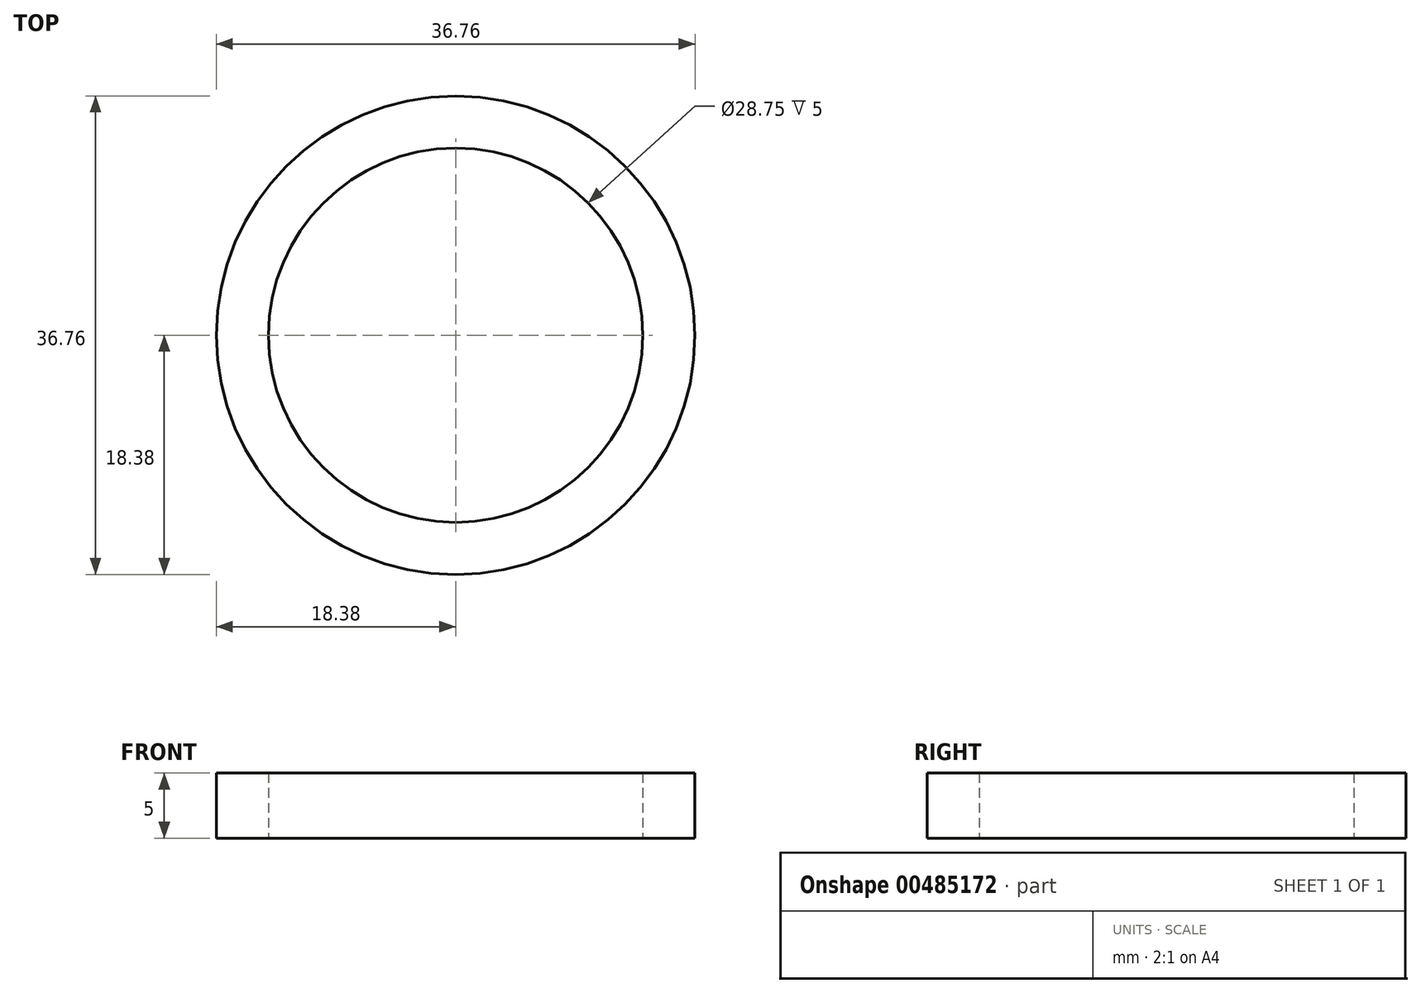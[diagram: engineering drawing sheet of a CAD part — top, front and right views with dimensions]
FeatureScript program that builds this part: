
annotation { "Feature Type Name" : "Feature", "Feature Type Description" : "" }
export const myFeature = defineFeature(function(context is Context, id is Id, definition is map)
    precondition{}
    {
        {
            var Q0;
            Q0=qCreatedBy(makeId("Top.planeOp"),FACE);
            var sketch = newSketch(context, id + "F0", { "sketchPlane" : qUnion([Q0])});
            skCircle(sketch, "E0", {"center": v(0, 0) * mm, "radius": 18.38 * mm});
            skCircle(sketch, "E1", {"center": v(0, 0) * mm, "radius": 14.38 * mm});
            skSolve(sketch);
        }
        {
            var Q0;
            Q0 = qSketchRegion(id + "F0", true);
            extrude(context, id + "F1", {"entities" : qUnion([Q0]), "depth" : 5 * mm, "offsetDistance" : 25 * mm});
        }
    });
